# Revit family: BOS-Leibungszarge-SinoPlanar-Tosd-STW_Familie
name_source: partatom
category: Türen
revit_build: Autodesk Revit 2017 (Build: 20160225_1515(x64)
units: mm (PartAtom-declared; Revit-internal decimal feet)

## family parameters
Basisbauteil = Wand
Beim Laden mit Abzugskörper schneiden = Nein
Gemeinsam genutzt = Nein
Immer vertikal = Ja
Raumberechnungspunkt = Ja

## types (3) — shared parameters
Allgemeine Informationen zu Stahlzargen = www.BestOfSteel.de/tools-downloads/technische-infos-rund-um-die-stahlzarge/
BBL1 Bandbezugslinie   Hinge Position 1 = 241 mm  [stored 0.790682 ft]
BE max. = 100 mm  [stored 0.328084 ft]
Bauelement = BOS Stahlzarge
Beschreibung = Leibungszarge SinoPlanar für Ständerwerk, stumpf
Dichtung 1 = Ja
Einfachfalz = Ja
FMB max. = 1341 mm  [stored 4.39961 ft]
FMB min. = 591 mm  [stored 1.93898 ft]
FMH max. = 2858 mm  [stored 9.37664 ft]
FMH min. = 1608 mm  [stored 5.27559 ft]
Falzaufschlag = 15 mm  [stored 0.0492126 ft]
Falzaufschlag gesamt = 15 mm  [stored 0.0492126 ft]
Funktion = Innen
GT max. = 650 mm  [stored 2.13255 ft]
GT min. = 131 mm  [stored 0.42979 ft]
Hersteller = BOS GmbH Best Of Steel, Lütkenfelde 4, D-48282 Emsdetten
Info-Texte sichtbar = Ja
Information in English = Nein
Material = grundiert, feuerverzinktes Feinblech nach DIN EN 10143
Material - Acrylfuge = <Nach Kategorie>
Material - Bänder = <Nach Kategorie>
Material - Dichtung = <Nach Kategorie>
Material - Drückergarnitur = <Nach Kategorie>
Material - Türblatt = <Nach Kategorie>
Material - Zarge = <Nach Kategorie>
Profil verschiebung = 25 mm  [stored 0.082021 ft]
Putzwinkel hinten = 3 mm  [stored 0.00984252 ft]
Putzwinkel vorne = 3 mm  [stored 0.00984252 ft]
Stumpf = Ja
Türblattstärke = 70 mm  [stored 0.229659 ft]
URL = www.BestOfSteel.de/stahlzargen/zargen-fuer-drehfluegeltueren/sino-zargen/
Umkantung hinten = 10 mm  [stored 0.0328084 ft]
Umkantung vorne = 20 mm  [stored 0.0656168 ft]
Wandstärke max. = 644 mm  [stored 2.11286 ft]
Wandstärke min. = 125 mm  [stored 0.410105 ft]
zero-valued in all types: Breite, Dicke, Rohbaubreite, Rohbauhöhe, Türblattstärke 1

## per-type parameters (varying)
| type | Aussteifungsprofil 1 | Aussteifungsprofil 2 | Falztiefe | Falztiefe gesamt | Modell | Tectus Bänder | Tosd | Tosd (verdeckt liegendes Band) | Tosd 40/30/15 | Türblattstärke 2 | Türblattstärke 3 | VX Bänder |
| Tosd 40/30/15 | Ja | Nein | 49.5 mm  [stored 0.162402 ft] | 49.5 mm  [stored 0.162402 ft] | Tosd 40/30/15 | Nein | Nein | Nein | Ja | 40 mm  [stored 0.131234 ft] | 30 mm  [stored 0.0984252 ft] | Ja |
| Tosd | Nein | Ja | 54.5 mm  [stored 0.178806 ft] | 54.5 mm  [stored 0.178806 ft] | Tosd | Nein | Ja | Nein | Nein | 45 mm  [stored 0.147638 ft] | 25 mm  [stored 0.082021 ft] | Ja |
| Tosd (verdeckt liegendes Band) | Nein | Ja | 54.5 mm  [stored 0.178806 ft] | 54.5 mm  [stored 0.178806 ft] | Tosd (verdeckt lliegendes Band) | Ja | Nein | Ja | Nein | 45 mm  [stored 0.147638 ft] | 25 mm  [stored 0.082021 ft] | Nein |

note: [stored X ft] marks values corroborated as IEEE doubles in the binary element streams (Revit-internal decimal feet)
